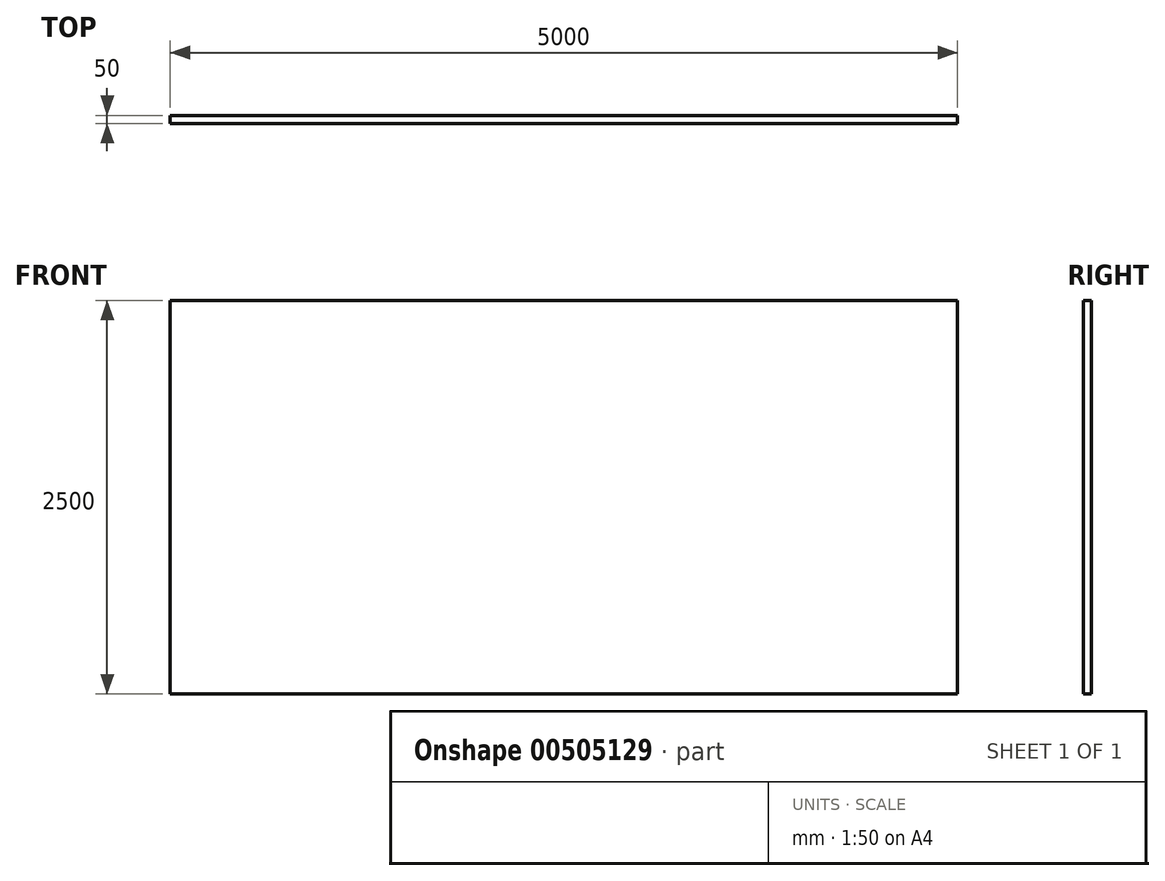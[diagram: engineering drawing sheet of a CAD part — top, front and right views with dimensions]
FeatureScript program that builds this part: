
annotation { "Feature Type Name" : "Feature", "Feature Type Description" : "" }
export const myFeature = defineFeature(function(context is Context, id is Id, definition is map)
    precondition{}
    {
        {
            var Q0;
            Q0=qCreatedBy(makeId("Front.planeOp"),FACE);
            var sketch = newSketch(context, id + "F0", { "sketchPlane" : qUnion([Q0])});
            skLineSegment(sketch, "E0.bottom", {"start": v(163.55, 0) * mm, "end": v(-4836.45, 0) * mm});
            skLineSegment(sketch, "E0.top", {"start": v(163.55, 2500) * mm, "end": v(-4836.45, 2500) * mm});
            skLineSegment(sketch, "E0.left", {"start": v(163.55, 0) * mm, "end": v(163.55, 2500) * mm});
            skLineSegment(sketch, "E0.right", {"start": v(-4836.45, 0) * mm, "end": v(-4836.45, 2500) * mm});
            skSolve(sketch);
        }
        {
            var Q0;
            Q0=makeQuery(id+"F0.imprint","IMPRINT",FACE,{"disambiguationData":[TD([[makeQuery(id+"F0.imprint","IMPRINT",EDGE,{"derivedFrom":sQuery(id+"F0.wireOp",EDGE,"E0.bottom")}),-1.0]])]});
            extrude(context, id + "F1", {"entities" : qUnion([Q0]), "depth" : 50 * mm});
        }
    });
